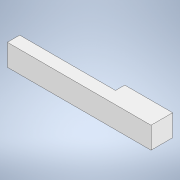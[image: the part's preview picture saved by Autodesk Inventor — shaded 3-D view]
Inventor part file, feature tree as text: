
AUTODESK INVENTOR PART (.ipt)
format: ipt  version: 2021 (Build 250183000, 183)  size: 96,768 bytes
history: native  units: in
note: dims shown in document units (in); Inventor stores cm internally (conversion verified against a paired STEP export)
features: extrude x1, sketch x1
ambient origin geometry x8: Origin, YZ Plane, XZ Plane, XY Plane, X Axis, Y Axis, Z Axis, Center Point
bodies: Solid1 (feature_tree)
feature tree (2):
  extrude  "Extrusion1"  Depth=5.8125in
  sketch  "Sketch1"  dims[d3=0.5in d4=5.8125in d5=0.875in d6=3.875in d7=0.875in d8=0.0in]
